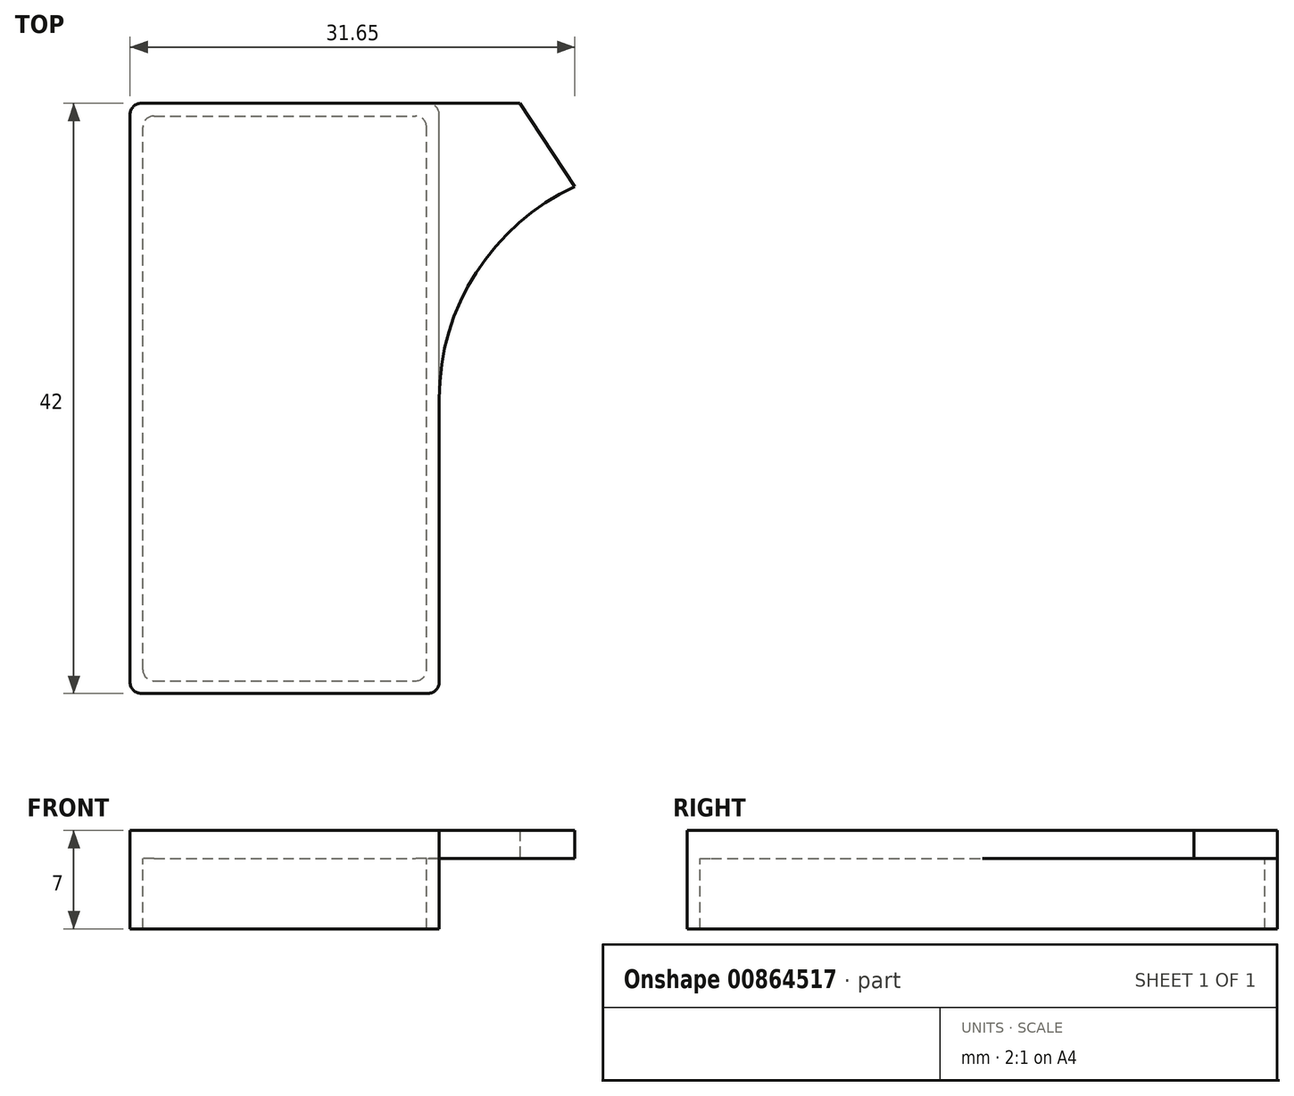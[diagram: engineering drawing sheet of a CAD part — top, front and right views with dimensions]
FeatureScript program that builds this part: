
annotation { "Feature Type Name" : "Feature", "Feature Type Description" : "" }
export const myFeature = defineFeature(function(context is Context, id is Id, definition is map)
    precondition{}
    {
        {
            var Q0;
            Q0=qCreatedBy(makeId("Top.planeOp"),FACE);
            var sketch = newSketch(context, id + "F0", { "sketchPlane" : qUnion([Q0])});
            skLineSegment(sketch, "E0.bottom", {"start": v(0, 0) * mm, "end": v(22, 0) * mm});
            skLineSegment(sketch, "E0.top", {"start": v(0, 42) * mm, "end": v(22, 42) * mm});
            skLineSegment(sketch, "E0.left", {"start": v(0, 0) * mm, "end": v(0, 42) * mm});
            skLineSegment(sketch, "E0.right", {"start": v(22, 0) * mm, "end": v(22, 42) * mm});
            skLineSegment(sketch, "E1.bottom", {"start": v(0.9, 0.9) * mm, "end": v(21.1, 0.9) * mm});
            skLineSegment(sketch, "E1.top", {"start": v(0.9, 41.1) * mm, "end": v(21.1, 41.1) * mm});
            skLineSegment(sketch, "E1.left", {"start": v(0.9, 0.9) * mm, "end": v(0.9, 41.1) * mm});
            skLineSegment(sketch, "E1.right", {"start": v(21.1, 0.9) * mm, "end": v(21.1, 41.1) * mm});
            skSolve(sketch);
        }
        {
            var Q0;
            Q0=makeQuery(id+"F0.imprint","IMPRINT",FACE,{"disambiguationData":[TD([[makeQuery(id+"F0.imprint","IMPRINT",EDGE,{"derivedFrom":sQuery(id+"F0.wireOp",EDGE,"E0.bottom")}),1.0]])]});
            extrude(context, id + "F1", {"entities" : qUnion([Q0]), "oppositeDirection" : true, "depth" : 5 * mm, "offsetDistance" : 25 * mm});
        }
        {
            var Q0;
            Q0=makeQuery(id+"F1.opExtrude","CAP_FACE",FACE,{"disambiguationData":[OSD([sQuery(id+"F0.wireOp",EDGE,"E0.bottom"),sQuery(id+"F0.wireOp",EDGE,"E0.top"),sQuery(id+"F0.wireOp",EDGE,"E0.left"),sQuery(id+"F0.wireOp",EDGE,"E0.right"),sQuery(id+"F0.wireOp",EDGE,"E1.bottom"),sQuery(id+"F0.wireOp",EDGE,"E1.top"),sQuery(id+"F0.wireOp",EDGE,"E1.left"),sQuery(id+"F0.wireOp",EDGE,"E1.right")])],"isStart":true});
            var sketch = newSketch(context, id + "F2", { "sketchPlane" : qUnion([Q0])});
            skLineSegment(sketch, "E2.bottom", {"start": v(0, 0) * mm, "end": v(22, 0) * mm});
            skLineSegment(sketch, "E2.top", {"start": v(0, 42) * mm, "end": v(22, 42) * mm});
            skLineSegment(sketch, "E2.left", {"start": v(0, 0) * mm, "end": v(0, 42) * mm});
            skLineSegment(sketch, "E2.right", {"start": v(22, 0) * mm, "end": v(22, 21) * mm});
            skLineSegment(sketch, "E3", {"start": v(22, 42) * mm, "end": v(27.75, 42) * mm});
            skLineSegment(sketch, "E4", {"start": v(27.75, 42) * mm, "end": v(31.65, 42) * mm, "construction": true});
            skLineSegment(sketch, "E5", {"start": v(31.65, 42) * mm, "end": v(31.65, 36.08) * mm, "construction": true});
            skLineSegment(sketch, "E6", {"start": v(27.75, 42) * mm, "end": v(31.65, 36.08) * mm});
            skArc(sketch, "E7", {"start": v(31.65, 36.08) * mm, "mid": v(24.62, 29.95) * mm, "end": v(22, 21) * mm});
            skSolve(sketch);
        }
        {
            var Q0;
            Q0=makeQuery(id+"F2.imprint","IMPRINT",FACE,{"disambiguationData":[TD([[makeQuery(id+"F2.imprint","IMPRINT",EDGE,{"derivedFrom":makeQuery(id+"F1.opExtrude","CAP_EDGE",EDGE,{"disambiguationData":[OSD([sQuery(id+"F0.wireOp",EDGE,"E1.bottom")])],"isStart":true})}),1.0]])]});
            var Q1;
            {var subQ0=sQuery(id+"F2.wireOp",EDGE,"E3");Q1=makeQuery(id+"F2.imprint","IMPRINT",FACE,{"disambiguationData":[TD([[makeQuery(id+"F2.imprint","IMPRINT",EDGE,{"derivedFrom":subQ0}),-1.0]])]});}
            var Q2;
            Q2=makeQuery(id+"F2.imprint","IMPRINT",FACE,{"disambiguationData":[TD([[makeQuery(id+"F2.imprint","IMPRINT",EDGE,{"derivedFrom":sQuery(id+"F2.wireOp",EDGE,"E2.bottom")}),1.0]])]});
            extrude(context, id + "F3", {"entities" : qUnion([Q0, Q1, Q2]), "operationType" : NewBodyOperationType.ADD, "depth" : 2 * mm, "offsetDistance" : 25 * mm});
        }
        {
            var Q0;
            Q0=makeQuery(id+"F3.boolean.opBoolean","MERGE",EDGE,{"derivedFrom":[makeQuery(id+"F1.opExtrude","SWEPT_EDGE",EDGE,{"disambiguationData":[OSD([sQuery(id+"F0.wireOp",EDGE,"E0.bottom"),sQuery(id+"F0.wireOp",EDGE,"E0.right")])]}),makeQuery(id+"F3.opExtrude","SWEPT_EDGE",EDGE,{"disambiguationData":[OSD([sQuery(id+"F2.wireOp",EDGE,"E2.bottom"),sQuery(id+"F2.wireOp",EDGE,"E2.right")])]})]});
            var Q1;
            Q1=makeQuery(id+"F3.boolean.opBoolean","MERGE",EDGE,{"derivedFrom":[makeQuery(id+"F1.opExtrude","SWEPT_EDGE",EDGE,{"disambiguationData":[OSD([sQuery(id+"F0.wireOp",EDGE,"E0.bottom"),sQuery(id+"F0.wireOp",EDGE,"E0.left")])]}),makeQuery(id+"F3.opExtrude","SWEPT_EDGE",EDGE,{"disambiguationData":[OSD([sQuery(id+"F2.wireOp",EDGE,"E2.bottom"),sQuery(id+"F2.wireOp",EDGE,"E2.left")])]})]});
            var Q2;
            Q2=makeQuery(id+"F3.boolean.opBoolean","MERGE",EDGE,{"derivedFrom":[makeQuery(id+"F1.opExtrude","SWEPT_EDGE",EDGE,{"disambiguationData":[OSD([sQuery(id+"F0.wireOp",EDGE,"E0.top"),sQuery(id+"F0.wireOp",EDGE,"E0.left")])]}),makeQuery(id+"F3.opExtrude","SWEPT_EDGE",EDGE,{"disambiguationData":[OSD([sQuery(id+"F2.wireOp",EDGE,"E2.top"),sQuery(id+"F2.wireOp",EDGE,"E2.left")])]})]});
            var Q3;
            Q3=makeQuery(id+"F1.opExtrude","SWEPT_EDGE",EDGE,{"disambiguationData":[OSD([sQuery(id+"F0.wireOp",EDGE,"E0.top"),sQuery(id+"F0.wireOp",EDGE,"E0.right")])]});
            var Q4;
            Q4=makeQuery(id+"F1.opExtrude","SWEPT_EDGE",EDGE,{"disambiguationData":[OSD([sQuery(id+"F0.wireOp",EDGE,"E1.bottom"),sQuery(id+"F0.wireOp",EDGE,"E1.right")])]});
            var Q5;
            Q5=makeQuery(id+"F1.opExtrude","SWEPT_EDGE",EDGE,{"disambiguationData":[OSD([sQuery(id+"F0.wireOp",EDGE,"E1.top"),sQuery(id+"F0.wireOp",EDGE,"E1.right")])]});
            var Q6;
            Q6=makeQuery(id+"F1.opExtrude","SWEPT_EDGE",EDGE,{"disambiguationData":[OSD([sQuery(id+"F0.wireOp",EDGE,"E1.bottom"),sQuery(id+"F0.wireOp",EDGE,"E1.left")])]});
            var Q7;
            Q7=makeQuery(id+"F1.opExtrude","SWEPT_EDGE",EDGE,{"disambiguationData":[OSD([sQuery(id+"F0.wireOp",EDGE,"E1.top"),sQuery(id+"F0.wireOp",EDGE,"E1.left")])]});
            fillet(context, id + "F4", {"entities" : qUnion([Q0, Q1, Q2, Q3, Q4, Q5, Q6, Q7]), "radius" : 0.8 * mm, "tangentPropagation" : true, "allowEdgeOverflow" : false});
        }
    });
